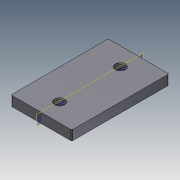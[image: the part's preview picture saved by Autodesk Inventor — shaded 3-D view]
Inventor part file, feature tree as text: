
AUTODESK INVENTOR PART (.ipt)
format: ipt  version: 2015 (Build 190159000, 159)  size: 113,664 bytes
history: native  units: mm
features: plane x2, sheet_metal_op x1, hole x1, mirror x1, chamfer x1, sketch x1, other x1
ambient origin geometry x8: Origin, YZ Plane, XZ Plane, XY Plane, X Axis, Y Axis, Z Axis, Center Point
bodies: Solid1 (feature_tree)
feature tree (8):
  sheet_metal_op  "Face1"
  hole  "Hole1"  [1 undecoded]
  plane  "Work Plane1"
  plane  "Work Plane2"
  mirror  "Mirror1"
  chamfer  "Corner Round1"
  sketch  "Sketch1"  dims[d2=80.0mm d3=50.0mm d4=0.001mm d5=15.0mm d6=25.0mm d7=8.376mm d8=6.0mm d9=4.0mm d10=2.0mm d11=90.0deg d12=8.0mm d13=20.594885mm d14=1.0mm]
  other  "Plate1"
note: 1 required parameter value undecoded (feature->parameter linkage not recoverable at this tier; creation-order binding heuristic only, values carry confidence <= 0.55)
